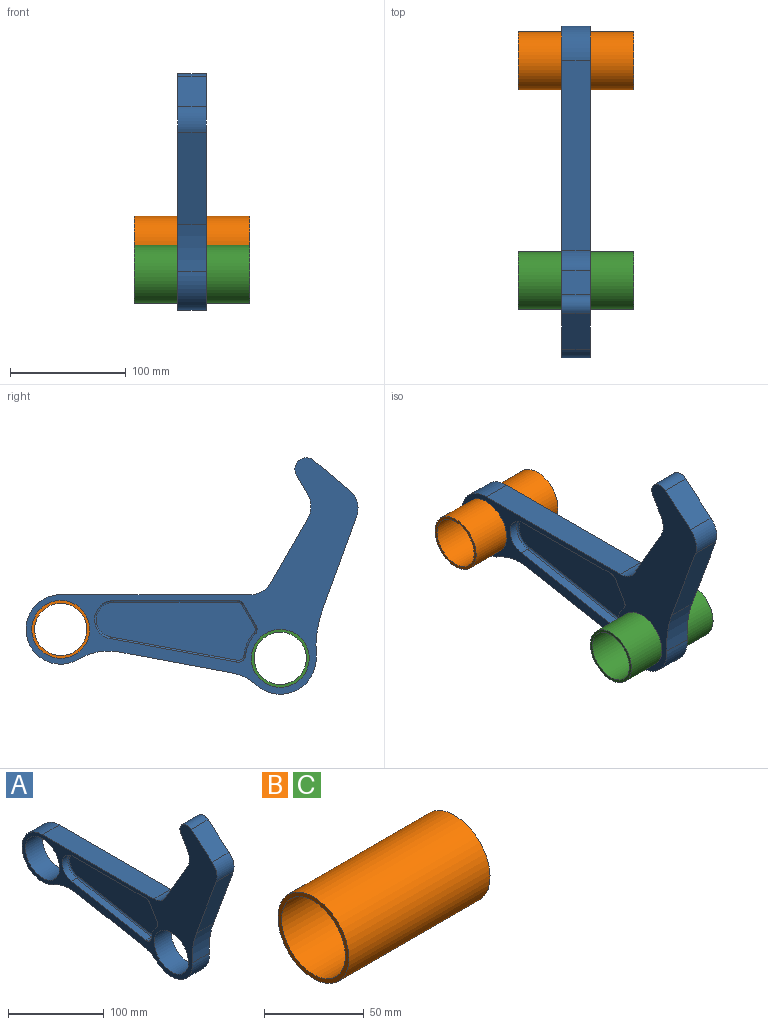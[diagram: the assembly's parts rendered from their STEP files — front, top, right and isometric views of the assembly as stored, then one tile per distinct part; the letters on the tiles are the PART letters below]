
ASSEMBLY  parts=3 mates=1
PART A: 53 faces, bbox 25x287.4x204.7 mm
  f0: plane 31.06x26.06mm, normal (0,-0.64,0.77), area 1013.5mm2, adj f1,f15,f17,f35
  f1: cylinder r=20mm len=25mm, axis (-1,0,0), area 610.9mm2, adj f0,f2,f17,f35
  f2: plane 80.26x29.21mm, normal (0,-0.94,-0.34), area 2135.2mm2, adj f1,f3,f17,f35
  f3: cylinder r=100mm len=40.74mm, axis (-1,0,0), area 1036.2mm2, adj f2,f4,f17,f35
  f4: cylinder r=31.1mm len=52.28mm, axis (-1,0,0), area 1854.8mm2, adj f3,f5,f17,f35
  f5: cylinder r=40mm len=25mm, axis (-1,0,0), area 566.3mm2, adj f4,f6,f17,f35
  f6: plane 98.49x25mm, normal (0,0.18,-0.98), area 2504.1mm2, adj f5,f7,f17,f35
  f7: cylinder r=50mm len=34.86mm, axis (-1,0,0), area 905.2mm2, adj f6,f8,f17,f35
  f8: cylinder r=30.1mm len=60.2mm, axis (-1,0,0), area 2771.2mm2, adj f7,f9,f17,f35
  f9: plane 164.08x25mm, normal (0,0,1), area 4101.9mm2, adj f8,f10,f17,f35
  f10: cylinder r=20mm len=25mm, axis (-1,0,0), area 523.6mm2, adj f9,f11,f17,f35
  f11: plane 56.3x32.51mm, normal (0,0.87,0.5), area 1625.2mm2, adj f10,f12,f17,f35
  f12: cylinder r=20mm len=25mm, axis (-1,0,0), area 523.6mm2, adj f11,f13,f17,f35
  f13: plane 25x17.19mm, normal (0,0.87,-0.5), area 496.1mm2, adj f12,f15,f17,f35
  f14: cylinder r=25.1mm len=50.2mm, axis (-1,0,0), area 3942.7mm2, adj f17,f35
  f15: cylinder r=10mm len=25mm, axis (-1,0,0), area 698.1mm2, adj f0,f13,f17,f35
  f16: cylinder r=25.1mm len=50.2mm, axis (-1,0,0), area 3942.7mm2, adj f17,f35
  f17: plane 287.37x204.69mm, normal (1,0,0), area 11088.1mm2, adj f0,f1,f2,f3,f4,f5,f6,f7
  f18: plane 18.49x10.67mm, normal (0,0.87,-0.5), area 170.8mm2, adj f17,f19,f25,f30
  f19: cylinder r=6.5mm len=8mm, axis (-1,0,0), area 66.6mm2, adj f17,f18,f20,f28
  f20: cylinder r=30.1mm len=18.03mm, axis (-1,0,0), area 161.1mm2, adj f17,f19,f21,f27
  f21: cylinder r=6.5mm len=8mm, axis (-1,0,0), area 86.7mm2, adj f17,f20,f22,f29
  f22: plane 109.5x20.27mm, normal (0,-0.18,0.98), area 890.9mm2, adj f17,f21,f23,f31
  f23: cylinder r=16.66mm len=33.03mm, axis (-1,0,0), area 394.2mm2, adj f17,f22,f24,f33
  f24: plane 106.82x8mm, normal (0,0,-1), area 854.5mm2, adj f17,f23,f25,f34
  f25: cylinder r=6.5mm len=8mm, axis (-1,0,0), area 54.5mm2, adj f17,f18,f24,f32
  f26: plane 137.65x50.41mm, normal (1,0,0), area 5147mm2, adj f27,f28,f29,f30,f31,f32,f33,f34
  f27: torus R=31.6mm, axis (1,0,0), area 48.3mm2, adj f20,f26,f28,f29
  f28: torus R=5mm, axis (1,0,0), area 18mm2, adj f19,f26,f27,f30
  f29: torus R=5mm, axis (1,0,0), area 23.4mm2, adj f21,f26,f27,f31
  f30: cylinder r=1.5mm len=19.24mm, axis (0,0.5,0.87), area 50.3mm2, adj f18,f26,f28,f32
  f31: cylinder r=1.5mm len=109.78mm, axis (0,-0.98,-0.18), area 262.4mm2, adj f22,f26,f29,f33
  f32: torus R=5mm, axis (1,0,0), area 14.7mm2, adj f25,f26,f30,f34
  f33: torus R=15.16mm, axis (1,0,0), area 112.3mm2, adj f23,f26,f31,f34
  f34: cylinder r=1.5mm len=106.82mm, axis (0,1,0), area 251.7mm2, adj f24,f26,f32,f33
  f35: plane 287.37x204.69mm, normal (-1,0,0), area 11088.1mm2, adj f0,f1,f2,f3,f4,f5,f6,f7
  f36: plane 18.49x10.67mm, normal (0,0.87,-0.5), area 170.8mm2, adj f35,f37,f43,f48
  f37: cylinder r=6.5mm len=8mm, axis (1,0,0), area 66.6mm2, adj f35,f36,f38,f46
  f38: cylinder r=30.1mm len=18.03mm, axis (1,0,0), area 161.1mm2, adj f35,f37,f39,f45
  f39: cylinder r=6.5mm len=8mm, axis (1,0,0), area 86.7mm2, adj f35,f38,f40,f47
  f40: plane 109.5x20.27mm, normal (0,-0.18,0.98), area 890.9mm2, adj f35,f39,f41,f49
  f41: cylinder r=16.66mm len=33.03mm, axis (1,0,0), area 394.2mm2, adj f35,f40,f42,f51
  f42: plane 106.82x8mm, normal (0,0,-1), area 854.5mm2, adj f35,f41,f43,f52
  f43: cylinder r=6.5mm len=8mm, axis (1,0,0), area 54.5mm2, adj f35,f36,f42,f50
  f44: plane 137.65x50.41mm, normal (-1,0,0), area 5147mm2, adj f45,f46,f47,f48,f49,f50,f51,f52
  f45: torus R=31.6mm, axis (-1,0,0), area 48.3mm2, adj f38,f44,f46,f47
  f46: torus R=5mm, axis (-1,0,0), area 18mm2, adj f37,f44,f45,f48
  f47: torus R=5mm, axis (-1,0,0), area 23.4mm2, adj f39,f44,f45,f49
  f48: cylinder r=1.5mm len=19.24mm, axis (0,0.5,0.87), area 50.3mm2, adj f36,f44,f46,f50
  f49: cylinder r=1.5mm len=109.78mm, axis (0,-0.98,-0.18), area 262.4mm2, adj f40,f44,f47,f51
  f50: torus R=5mm, axis (-1,0,0), area 14.7mm2, adj f43,f44,f48,f52
  f51: torus R=15.16mm, axis (-1,0,0), area 112.3mm2, adj f41,f44,f49,f52
  f52: cylinder r=1.5mm len=106.82mm, axis (0,1,0), area 251.7mm2, adj f42,f44,f50,f51
PART B: 4 faces, bbox 100x50.2x50.2 mm
  f0: cylinder r=25.1mm len=100mm, axis (-1,0,0), area 15770.8mm2, adj f1,f2
  f1: plane 50.2x50.2mm, normal (1,0,0), area 374.6mm2, adj f0,f3
  f2: plane 50.2x50.2mm, normal (-1,0,0), area 374.6mm2, adj f0,f3
  f3: cylinder r=22.6mm len=100mm, axis (-1,0,0), area 14200mm2, adj f1,f2
PART C: same geometry as B
PLACE A at identity fixed
PLACE B t=(0,190,25)mm
PLACE C at identity
MATE slider B.f0 <-> A.f14  axis (-1,0,0) through (0,0,0)mm
